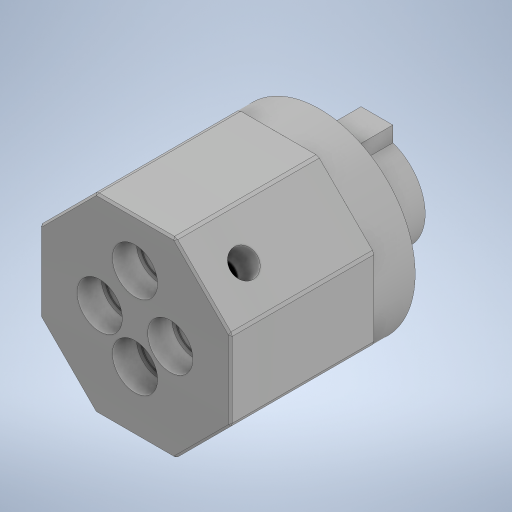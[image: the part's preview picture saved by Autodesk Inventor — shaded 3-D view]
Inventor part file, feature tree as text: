
AUTODESK INVENTOR PART (.ipt)
format: ipt  version: 2023.4 (Build 274418000, 418)  size: 458,240 bytes
history: native  units: mm
features: extrude x8, chamfer x5, sketch x4
ambient origin geometry x8: Origin, YZ Plane, XZ Plane, XY Plane, X Axis, Y Axis, Z Axis, Center Point
bodies: Solid1 (feature_tree)
feature tree (17):
  extrude  "Extrusion1"  Depth=2.5mm
  extrude  "Extrusion2"  Depth=2.0mm
  extrude  "Extrusion3"  Depth=30.0mm
  chamfer  "Chamfer1"  Distance=5.5mm
  extrude  "Extrusion4"  Depth=1.0mm TaperAngle=0.0deg
  extrude  "Extrusion5"  Depth=1.0mm TaperAngle=45.0deg
  extrude  "Extrusion6"  Depth=2.0mm
  chamfer  "Chamfer2"  Distance=15.0mm
  chamfer  "Chamfer3"  Distance=4.0mm
  chamfer  "Chamfer4"  Distance=11.1mm
  extrude  "Extrusion7"  Depth=2.0mm
  extrude  "Extrusion8"  Depth=2.0mm
  chamfer  "Chamfer5"  Distance=40.0mm Angle=360.0deg
  sketch  "Sketch1"  dims[d0=15.15mm d1=2.5mm]
  sketch  "Sketch4"  dims[d2=5.0mm d3=2.0mm]
  sketch  "Sketch5"  dims[d4=10.0mm d5=0.0mm d6=30.0mm d7=5.5mm d8=0.0mm]
  sketch  "Sketch9"  dims[d9=27.0mm d10=1.0mm d11=0.0mm d12=1.0mm d13=2.0mm d14=45.0deg d15=4.0mm d16=15.0mm d17=4.0mm d18=11.1mm d19=0.5mm d20=0.5mm d21=40.0mm d23=360.0deg d25=0.0mm d26=0.0mm d27=45.0deg d28=80.0mm d30=360.0deg d32=22.55mm d33=0.0mm d34=7.1mm d35=7.1mm d36=7.1mm d37=7.1mm d38=4.1mm d39=0.0mm d40=0.3mm d41=2.0mm d42=45.0deg d43=1.0mm d44=2.0mm d45=45.0deg d46=0.3mm d47=2.0mm d48=45.0deg d49=4.2mm d50=6.5mm d51=11.826407mm d52=5.913203mm d53=5.0mm d54=0.0mm d55=3.0mm d56=3.0mm d57=3.0mm d58=3.0mm d59=30.55mm d60=0.0mm d61=0.5mm d62=2.0mm d63=45.0deg]
